# Revit family: Hekatron_Feststellanlagen_THM 455 Ex_DE_22.01
name_source: partatom
category: Brandmelder
revit_build: Autodesk Revit 2018 (Build: 20190510_1515(x64)
units: mm (PartAtom-declared; Revit-internal decimal feet)

## family parameters
Basisbauteil = Fläche
Beim Laden mit Abzugskörper schneiden = Nein
Bemaßung runder Anschluss = Durchmesser verwenden
Beschriftungsausrichtung beibehalten = Ja
Gemeinsam genutzt = Nein
OmniClass-Nummer = 23.85.30.21
OmniClass-Titel = Environmental Detection/Registration
Raumberechnungspunkt = Nein
Teiletyp = Normal

## types (1)
- THM 455 Ex
    Beschreibung = Türhaftmagnet für Feststellanlagen an Brand- und Rauchschutztüren- und toren in den Ex-Zonen 1, 2 und 21, 22. Mit Verpolschutz und Löschdiode. Gemäß ATEX. Passend zur Ankerplatte ASV 75.
    Betriebsspannung = 24 V DC
    Breite (mm) = 52.0
    EG-Konformitätszertifikat / Zertifikat der Leistungsbeständigkeit = 0786-CPR-21628
    Ex-Zonen = 1, 2, 21, 22
    Farbe = metall
    Hersteller = Hekatron
    Höhe (mm) = 105.0
    Kabeleinführung = unten
    Leistungserklärung (DoP) = CPR-31-19-505
    Link zu Ausschreibungstext = https://www.meinhplus.de
    Link zu ausschreiben.de = http://www.ausschreiben.de
    Material = Metall
    Modell = THM 455 Ex
    Montageart = Aufputz
    Schutzart = IP 65
    Stromaufnahme = max. 125mA
    Tiefe (mm) = 75.0
    Typenkommentare = Türhaftmagnet THM 455 Ex
    UB A&S Artikel Nummer = 31-6500001-01-01
    URL = https://www.hekatron-brandschutz.de
    Version des BIM Objektes = 22.01
    Vorgabe-Ansicht = 1200 mm
    Zulässige Umgebungstemperatur = -20 °C bis +40 °C

## geometry (parser evidence)
native form markers: Sweep x2
no freeform markers — native parametric forms only
